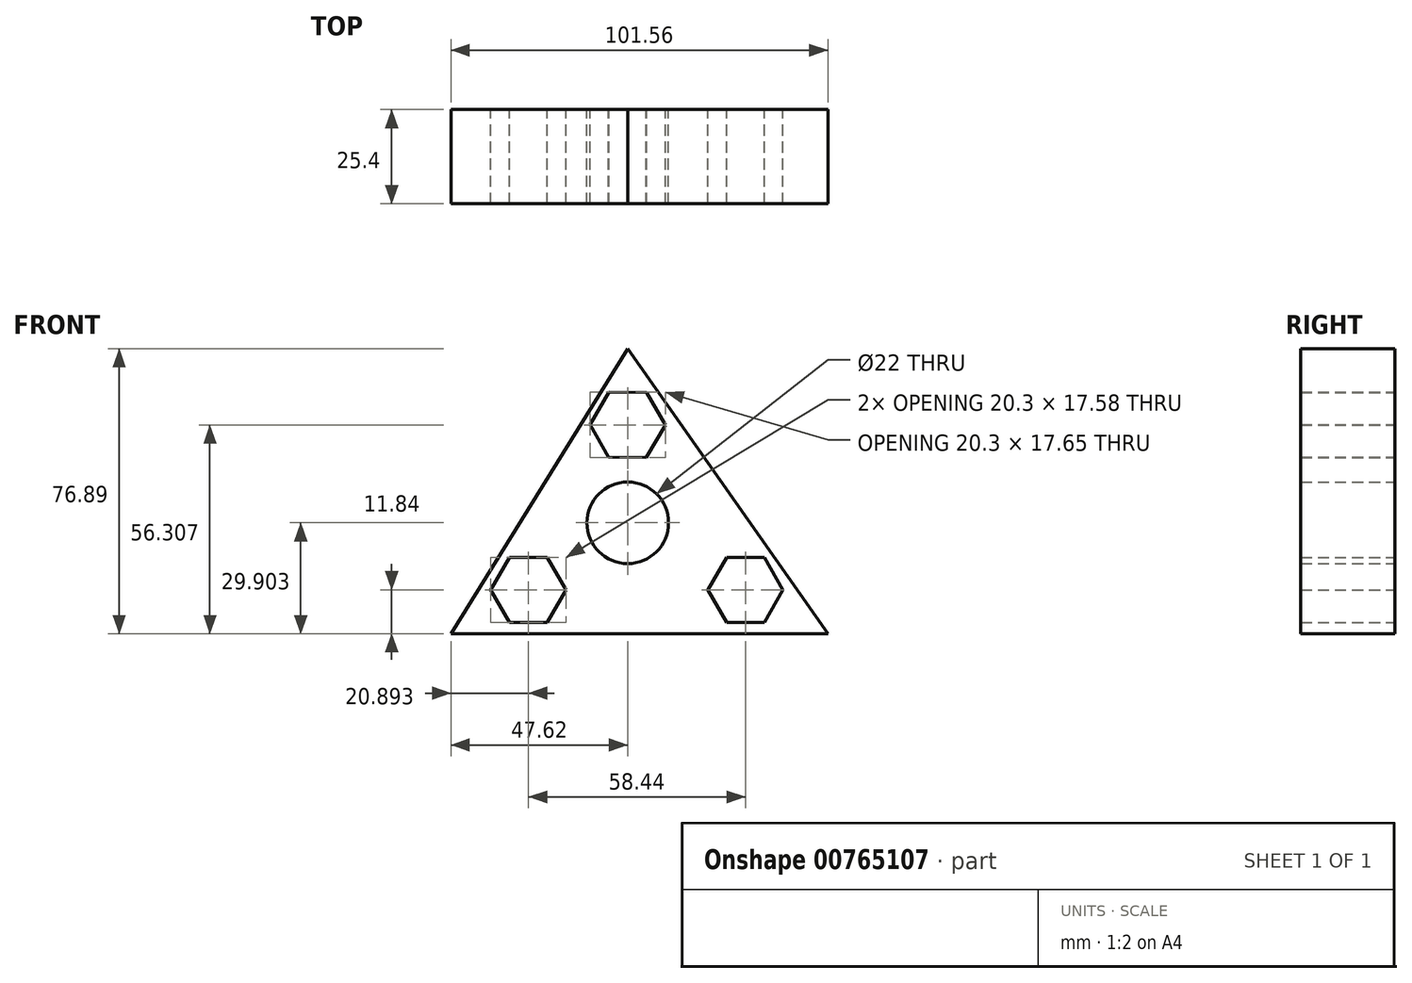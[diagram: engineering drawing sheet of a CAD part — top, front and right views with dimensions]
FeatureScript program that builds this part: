
annotation { "Feature Type Name" : "Feature", "Feature Type Description" : "" }
export const myFeature = defineFeature(function(context is Context, id is Id, definition is map)
    precondition{}
    {
        {
            var Q0;
            Q0=qCreatedBy(makeId("Front.planeOp"),FACE);
            var sketch = newSketch(context, id + "F0", { "sketchPlane" : qUnion([Q0])});
            skCircle(sketch, "E0", {"center": v(0, 18.06) * mm, "radius": 11 * mm});
            skCircle(sketch, "E1", {"center": v(0, 18.06) * mm, "radius": 9.3 * mm});
            skCircle(sketch, "E2", {"center": v(0, 18.06) * mm, "radius": 4 * mm});
            skLineSegment(sketch, "E3.0", {"start": v(68.17, 9.92) * mm, "end": v(68.17, 9.92) * mm});
            skCircle(sketch, "E4.cCircle", {"center": v(0, 44.47) * mm, "radius": 8.79 * mm, "construction": true});
            skLineSegment(sketch, "E4.0", {"start": v(5.14, 53.22) * mm, "end": v(10.15, 44.39) * mm});
            skLineSegment(sketch, "E4.1", {"start": v(10.15, 44.39) * mm, "end": v(5, 35.64) * mm});
            skLineSegment(sketch, "E4.2", {"start": v(5, 35.64) * mm, "end": v(-5.14, 35.72) * mm});
            skLineSegment(sketch, "E4.3", {"start": v(-5.14, 35.72) * mm, "end": v(-10.15, 44.55) * mm});
            skLineSegment(sketch, "E4.4", {"start": v(-10.15, 44.55) * mm, "end": v(-5, 53.3) * mm});
            skLineSegment(sketch, "E4.5", {"start": v(-5, 53.3) * mm, "end": v(5.14, 53.22) * mm});
            skPoint(sketch, "E4.0.midPoint", {"position": v(7.64, 48.8) * mm});
            skCircle(sketch, "E5.cCircle", {"center": v(31.71, 0) * mm, "radius": 8.79 * mm, "construction": true});
            skLineSegment(sketch, "E5.0", {"start": v(36.79, -8.79) * mm, "end": v(26.64, -8.79) * mm});
            skLineSegment(sketch, "E5.1", {"start": v(26.64, -8.79) * mm, "end": v(21.56, 0) * mm});
            skLineSegment(sketch, "E5.2", {"start": v(21.56, 0) * mm, "end": v(26.64, 8.79) * mm});
            skLineSegment(sketch, "E5.3", {"start": v(26.64, 8.79) * mm, "end": v(36.79, 8.79) * mm});
            skLineSegment(sketch, "E5.4", {"start": v(36.79, 8.79) * mm, "end": v(41.86, 0) * mm});
            skLineSegment(sketch, "E5.5", {"start": v(41.86, 0) * mm, "end": v(36.79, -8.79) * mm});
            skPoint(sketch, "E5.0.midPoint", {"position": v(31.71, -8.79) * mm});
            skCircle(sketch, "E6.cCircle", {"center": v(-26.73, 0) * mm, "radius": 8.79 * mm, "construction": true});
            skLineSegment(sketch, "E6.0", {"start": v(-21.65, -8.79) * mm, "end": v(-31.8, -8.79) * mm});
            skLineSegment(sketch, "E6.1", {"start": v(-31.8, -8.79) * mm, "end": v(-36.88, 0) * mm});
            skLineSegment(sketch, "E6.2", {"start": v(-36.88, 0) * mm, "end": v(-31.8, 8.79) * mm});
            skLineSegment(sketch, "E6.3", {"start": v(-31.8, 8.79) * mm, "end": v(-21.65, 8.79) * mm});
            skLineSegment(sketch, "E6.4", {"start": v(-21.65, 8.79) * mm, "end": v(-16.58, 0) * mm});
            skLineSegment(sketch, "E6.5", {"start": v(-16.58, 0) * mm, "end": v(-21.65, -8.79) * mm});
            skPoint(sketch, "E6.0.midPoint", {"position": v(-26.73, -8.79) * mm});
            skLineSegment(sketch, "E7", {"start": v(-26.73, -8.79) * mm, "end": v(-21.65, -8.79) * mm});
            skLineSegment(sketch, "E8.trimOffspring", {"start": v(26.64, -8.79) * mm, "end": v(36.79, -8.79) * mm});
            skLineSegment(sketch, "E9", {"start": v(-31.8, -8.79) * mm, "end": v(-21.65, -8.79) * mm});
            skLineSegment(sketch, "E10", {"start": v(-36.88, 0) * mm, "end": v(-31.8, -8.79) * mm});
            skLineSegment(sketch, "E11", {"start": v(41.86, 0) * mm, "end": v(36.79, 8.79) * mm});
            skLineSegment(sketch, "E12", {"start": v(36.79, 8.79) * mm, "end": v(26.64, 8.79) * mm});
            skLineSegment(sketch, "E13.trimOffspring", {"start": v(26.64, -8.79) * mm, "end": v(31.71, -8.79) * mm});
            skLineSegment(sketch, "E14", {"start": v(0, 65.05) * mm, "end": v(-47.62, -11.84) * mm});
            skLineSegment(sketch, "E15", {"start": v(-47.62, -11.84) * mm, "end": v(53.94, -11.84) * mm});
            skLineSegment(sketch, "E16", {"start": v(53.94, -11.84) * mm, "end": v(0, 65.05) * mm});
            skSolve(sketch);
        }
        {
            var Q0;
            Q0=makeQuery(id+"F0.imprint","IMPRINT",FACE,{"disambiguationData":[TD([[makeQuery(id+"F0.imprint","IMPRINT",EDGE,{"derivedFrom":sQuery(id+"F0.wireOp",EDGE,"E0")}),-1.0]])]});
            extrude(context, id + "F1", {"entities" : qUnion([Q0]), "depth" : 25.4 * mm, "offsetDistance" : 25.4 * mm});
        }
        {
            var Q0;
            Q0 = qSketchRegion(id + "F0", true);
            extrude(context, id + "F2", {"entities" : qUnion([Q0]), "operationType" : NewBodyOperationType.ADD, "depth" : 25.4 * mm, "offsetDistance" : 25.4 * mm});
        }
    });
